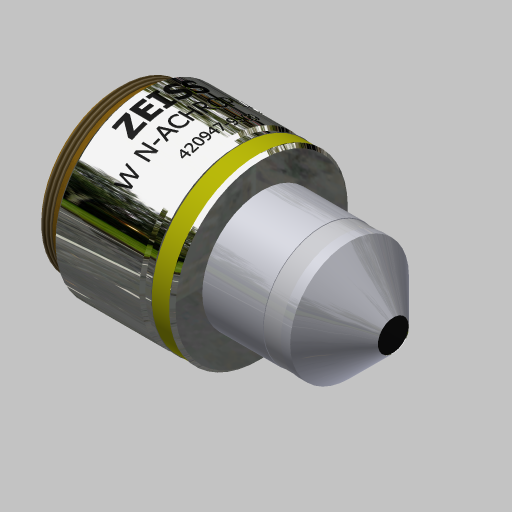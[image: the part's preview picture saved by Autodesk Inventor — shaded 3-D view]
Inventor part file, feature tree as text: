
AUTODESK INVENTOR PART (.ipt)
format: ipt  version: 2023 (Build 270158000, 158)  size: 5,100,032 bytes
history: native  units: mm
features: other x5, sketch x3, plane x2, hole x2, revolve x1, chamfer x1, thread x1
ambient origin geometry x8: Origin, YZ Plane, XZ Plane, XY Plane, X Axis, Y Axis, Z Axis, Center Point
bodies: Body1 (feature_tree)
feature tree (15):
  sketch  "Sketch1"  dims[d10=15.0mm]
  other  "Work Axis1"
  other  "Work Point1"
  other  "back focal plane"
  revolve  "Umdrehung3"
  chamfer  "Fase1"  Distance=20.2mm
  thread  "Gewinde3"  [1 undecoded]
  plane  "Arbeitsebene2"
  other  "Prägen1"
  hole  "Hole2"  [1 undecoded]
  hole  "Hole3"  [1 undecoded]
  plane  "Arbeitsebene3"
  other  "Prägen2"
  sketch  "Skizze2"  dims[d12=3.9mm]
  sketch  "Skizze3"  dims[d13=46.3mm d14=20.2mm d15=5.0mm d16=2.625mm d19=0.5mm d20=1.0mm d21=0.5mm d22=1.0mm d26=0.1mm d27=3.0mm d28=90.0deg d29=0.5mm d30=2.0mm d31=45.0deg d32=10.0mm d33=0.0mm d34=0.5mm d35=0.1mm d36=0.0mm d37=10.0mm d38=10.0mm d39=12.0mm d40=6.0mm d41=4.0mm d42=2.0mm d43=90.0deg d44=6.9mm d45=0.0mm d62=10.0mm d63=10.0mm d48=5.25mm d49=6.0mm d50=4.0mm d51=2.0mm d52=90.0deg d53=0.1mm d54=0.0mm d55=0.1mm d56=0.0mm d58=15.1mm d59=35.0mm d60=0.1mm d61=3.0mm d64=7.870902mm]
note: 3 required parameter values undecoded (feature->parameter linkage not recoverable at this tier; creation-order binding heuristic only, values carry confidence <= 0.55)
